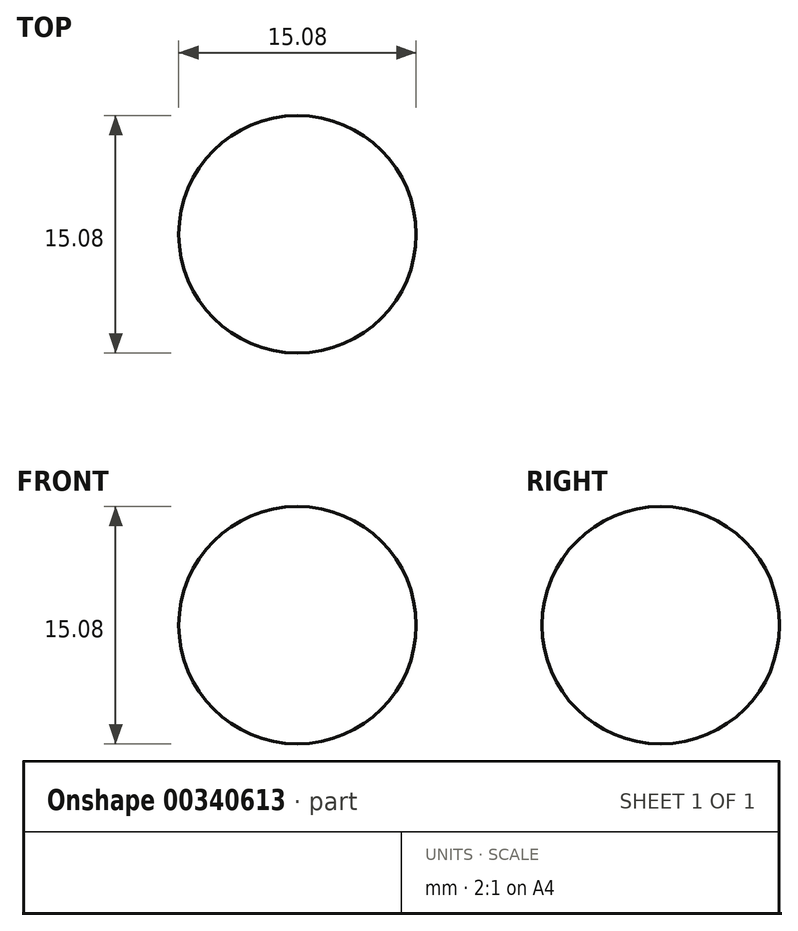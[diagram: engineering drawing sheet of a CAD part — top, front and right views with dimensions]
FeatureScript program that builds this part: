
annotation { "Feature Type Name" : "Feature", "Feature Type Description" : "" }
export const myFeature = defineFeature(function(context is Context, id is Id, definition is map)
    precondition{}
    {
        {
            var Q0;
            Q0=qCreatedBy(makeId("Right.planeOp"),FACE);
            var sketch = newSketch(context, id + "F0", { "sketchPlane" : qUnion([Q0])});
            skArc(sketch, "E0", {"start": v(0, 15.08) * mm, "mid": v(-7.54, 7.54) * mm, "end": v(0, 0) * mm});
            skLineSegment(sketch, "E1", {"start": v(0, 15.08) * mm, "end": v(0, 0) * mm});
            skSolve(sketch);
        }
        {
            var Q0;
            Q0=makeQuery(id+"F0.imprint","IMPRINT",FACE,{"disambiguationData":[TD([[makeQuery(id+"F0.imprint","IMPRINT",EDGE,{"derivedFrom":sQuery(id+"F0.wireOp",EDGE,"E0")}),1.0]])]});
            var Q1;
            Q1=sQuery(id+"F0.wireOp",EDGE,"E1");
            revolve(context, id + "F1", {"entities" : qUnion([Q0]), "axis" : qUnion([Q1]), "revolveType" : RevolveType.FULL});
        }
    });
